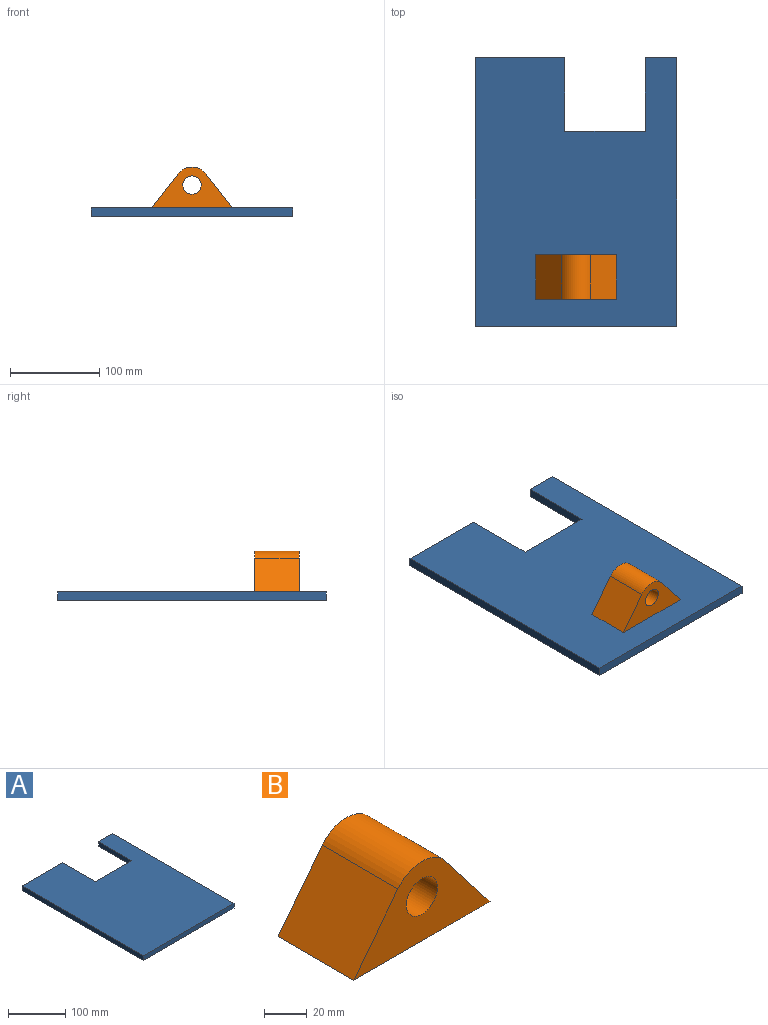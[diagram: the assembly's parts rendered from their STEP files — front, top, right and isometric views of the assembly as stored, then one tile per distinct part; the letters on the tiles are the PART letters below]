
ASSEMBLY  parts=2 mates=1
PART A: 10 faces, bbox 225x300x10 mm
  f0: plane 100x10mm, normal (0,1,0), area 1000mm2, adj f1,f7,f8,f9
  f1: plane 82x10mm, normal (1,0,0), area 820mm2, adj f0,f2,f8,f9
  f2: plane 90x10mm, normal (0,1,0), area 900mm2, adj f1,f3,f8,f9
  f3: plane 82x10mm, normal (-1,0,0), area 820mm2, adj f2,f4,f8,f9
  f4: plane 35x10mm, normal (0,1,0), area 350mm2, adj f3,f5,f8,f9
  f5: plane 300x10mm, normal (1,0,0), area 3000mm2, adj f4,f6,f8,f9
  f6: plane 225x10mm, normal (0,-1,0), area 2250mm2, adj f5,f7,f8,f9
  f7: plane 300x10mm, normal (-1,0,0), area 3000mm2, adj f0,f6,f8,f9
  f8: plane 300x225mm, normal (0,0,-1), area 60120mm2, adj f0,f1,f2,f3,f4,f5,f6,f7
  f9: plane 300x225mm, normal (0,0,1), area 60120mm2, adj f0,f1,f2,f3,f4,f5,f6,f7
PART B: 7 faces, bbox 90x50x45.5 mm
  f0: cylinder r=20mm len=50mm, axis (0,1,0), area 1825.1mm2, adj f1,f4,f5,f6
  f1: plane 50x37.73mm, normal (-0.79,0,0.61), area 2385mm2, adj f0,f2,f5,f6
  f2: plane 90x50mm, normal (0,0,-1), area 4500mm2, adj f1,f4,f5,f6
  f3: cylinder r=10.25mm len=50mm, axis (0,1,0), area 3220.1mm2, adj f5,f6
  f4: plane 50x37.73mm, normal (0.79,0,0.61), area 2385mm2, adj f0,f2,f5,f6
  f5: plane 90x45.5mm, normal (0,-1,0), area 2136.5mm2, adj f0,f1,f2,f3,f4
  f6: plane 90x45.5mm, normal (0,1,0), area 2136.5mm2, adj f0,f1,f2,f3,f4
PLACE A t=(-2.57,-174.1,-8.01)mm fixed
PLACE B t=(-32.87,-472.1,-5.01)mm
MATE fastened A.f9 <-> B.f2  axis (0,0,1) through (-35.07,-552.1,774.99)mm
